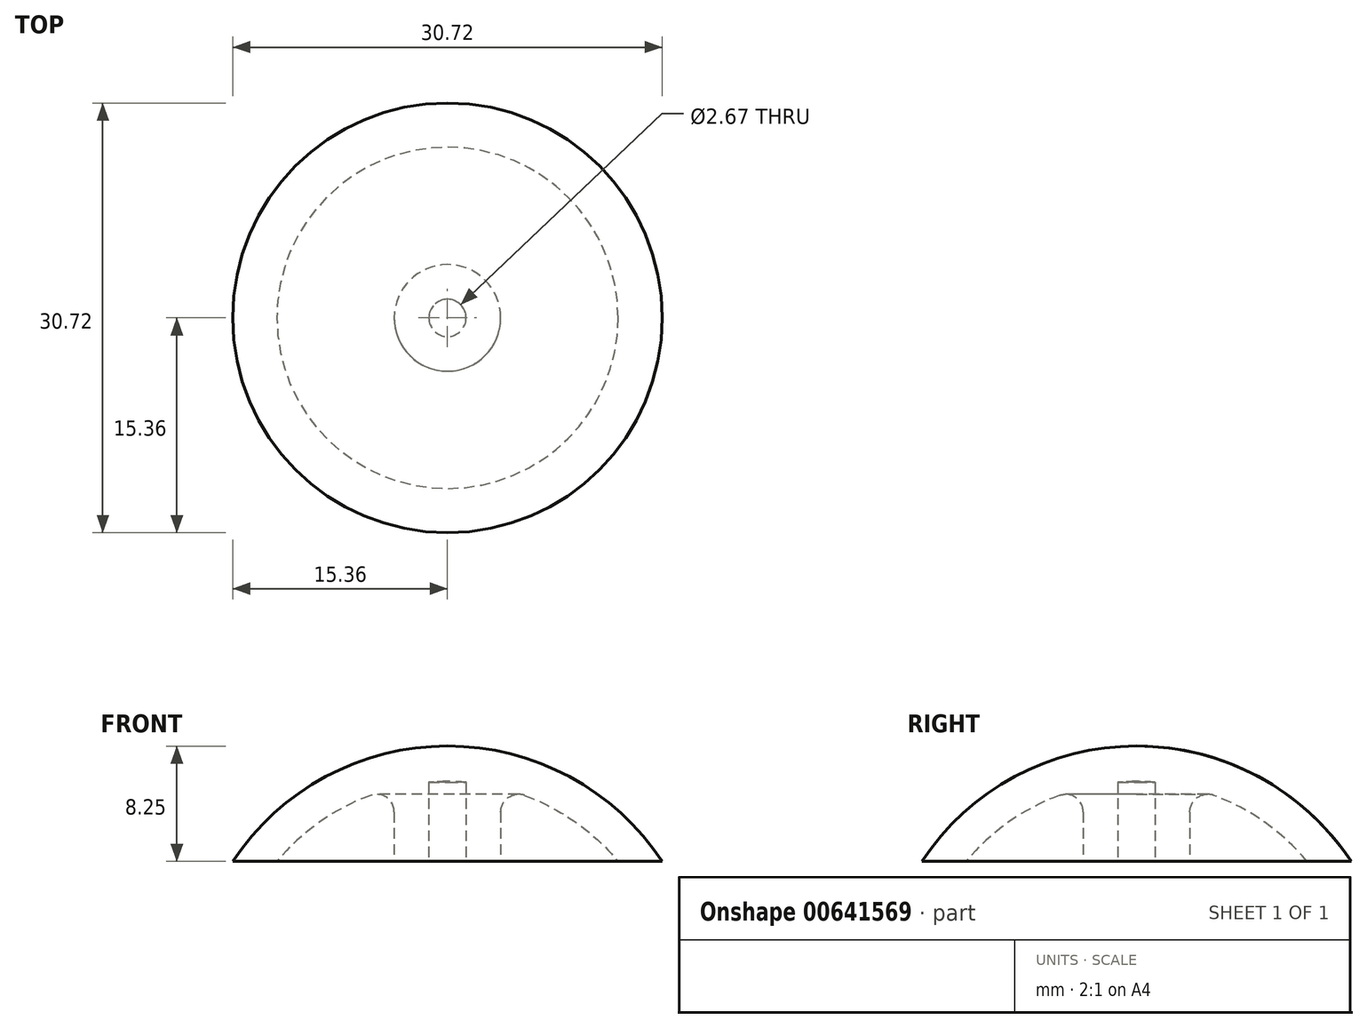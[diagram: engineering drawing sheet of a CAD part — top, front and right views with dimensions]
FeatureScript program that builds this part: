
annotation { "Feature Type Name" : "Feature", "Feature Type Description" : "" }
export const myFeature = defineFeature(function(context is Context, id is Id, definition is map)
    precondition{}
    {
        {
            var Q0;
            Q0=qCreatedBy(makeId("Top.planeOp"),FACE);
            var sketch = newSketch(context, id + "F0", { "sketchPlane" : qUnion([Q0])});
            skCircle(sketch, "E0", {"center": v(0, 0) * mm, "radius": 18.41 * mm});
            skSolve(sketch);
        }
        {
            var Q0;
            Q0=qCreatedBy(makeId("Right.planeOp"),FACE);
            var sketch = newSketch(context, id + "F1", { "sketchPlane" : qUnion([Q0])});
            skLineSegment(sketch, "E1", {"start": v(0, 0) * mm, "end": v(0, 18.41) * mm});
            skLineSegment(sketch, "E2", {"start": v(0, 0) * mm, "end": v(18.41, 0) * mm});
            skArc(sketch, "E3", {"start": v(18.41, 0) * mm, "mid": v(13.02, 13.02) * mm, "end": v(0, 18.41) * mm});
            skSolve(sketch);
        }
        {
            var Q0;
            Q0=qSketchRegion(id+"F1",true);
            var Q1;
            Q1=sQuery(id+"F1.wireOp",EDGE,"E1");
            revolve(context, id + "F2", {"entities" : qUnion([Q0]), "axis" : qUnion([Q1]), "revolveType" : RevolveType.FULL});
        }
        {
            var Q0;
            Q0=makeQuery(id+"F2.opRevolve","SWEPT_FACE",FACE,{"disambiguationData":[OSD([sQuery(id+"F1.wireOp",EDGE,"E2")])]});
            shell(context, id + "F3", {"entities" : qUnion([Q0]), "thickness" : 2.54 * mm});
        }
        {
            var Q0;
            Q0=makeQuery(id+"F0.imprint","IMPRINT",FACE,{"disambiguationData":[TD([[makeQuery(id+"F0.imprint","IMPRINT",EDGE,{"derivedFrom":sQuery(id+"F0.wireOp",EDGE,"E0")}),1.0]])]});
            var sketch = newSketch(context, id + "F4", { "sketchPlane" : qUnion([Q0])});
            skCircle(sketch, "E4", {"center": v(0, 0) * mm, "radius": 3.81 * mm});
            skCircle(sketch, "E5", {"center": v(0, 0) * mm, "radius": 1.33 * mm});
            skSolve(sketch);
        }
        {
            var Q0;
            Q0=qSketchRegion(id+"F4",true);
            var Q1;
            Q1=makeQuery(id+"F3.opShell","OFFSET_FACE",FACE,{"disambiguationData":[OSD([sQuery(id+"F1.wireOp",EDGE,"E3")])]});
            extrude(context, id + "F5", {"entities" : qUnion([Q0]), "operationType" : NewBodyOperationType.ADD, "endBound" : BoundingType.UP_TO_SURFACE, "depth" : 25.4 * mm, "endBoundEntityFace" : qUnion([Q1]), "offsetDistance" : 25.4 * mm});
        }
        {
            var Q0;
            Q0=makeQuery(id+"F5.opExtrude","CAP_EDGE",EDGE,{"disambiguationData":[OSD([sQuery(id+"F4.wireOp",EDGE,"E4")])],"isStart":false});
            fillet(context, id + "F6", {"entities" : qUnion([Q0]), "radius" : 1.27 * mm, "tangentPropagation" : true, "allowEdgeOverflow" : false});
        }
        {
            var Q0;
            Q0=makeQuery(id+"F0.imprint","IMPRINT",FACE,{"disambiguationData":[TD([[makeQuery(id+"F0.imprint","IMPRINT",EDGE,{"derivedFrom":sQuery(id+"F0.wireOp",EDGE,"E0")}),1.0]])]});
            var sketch = newSketch(context, id + "F7", { "sketchPlane" : qUnion([Q0])});
            skCircle(sketch, "E6", {"center": v(0, 0) * mm, "radius": 18.41 * mm});
            skSolve(sketch);
        }
        {
            var Q0;
            Q0=qSketchRegion(id+"F7",true);
            extrude(context, id + "F8", {"entities" : qUnion([Q0]), "operationType" : NewBodyOperationType.REMOVE, "depth" : 10.16 * mm, "offsetDistance" : 25.4 * mm});
        }
    });
